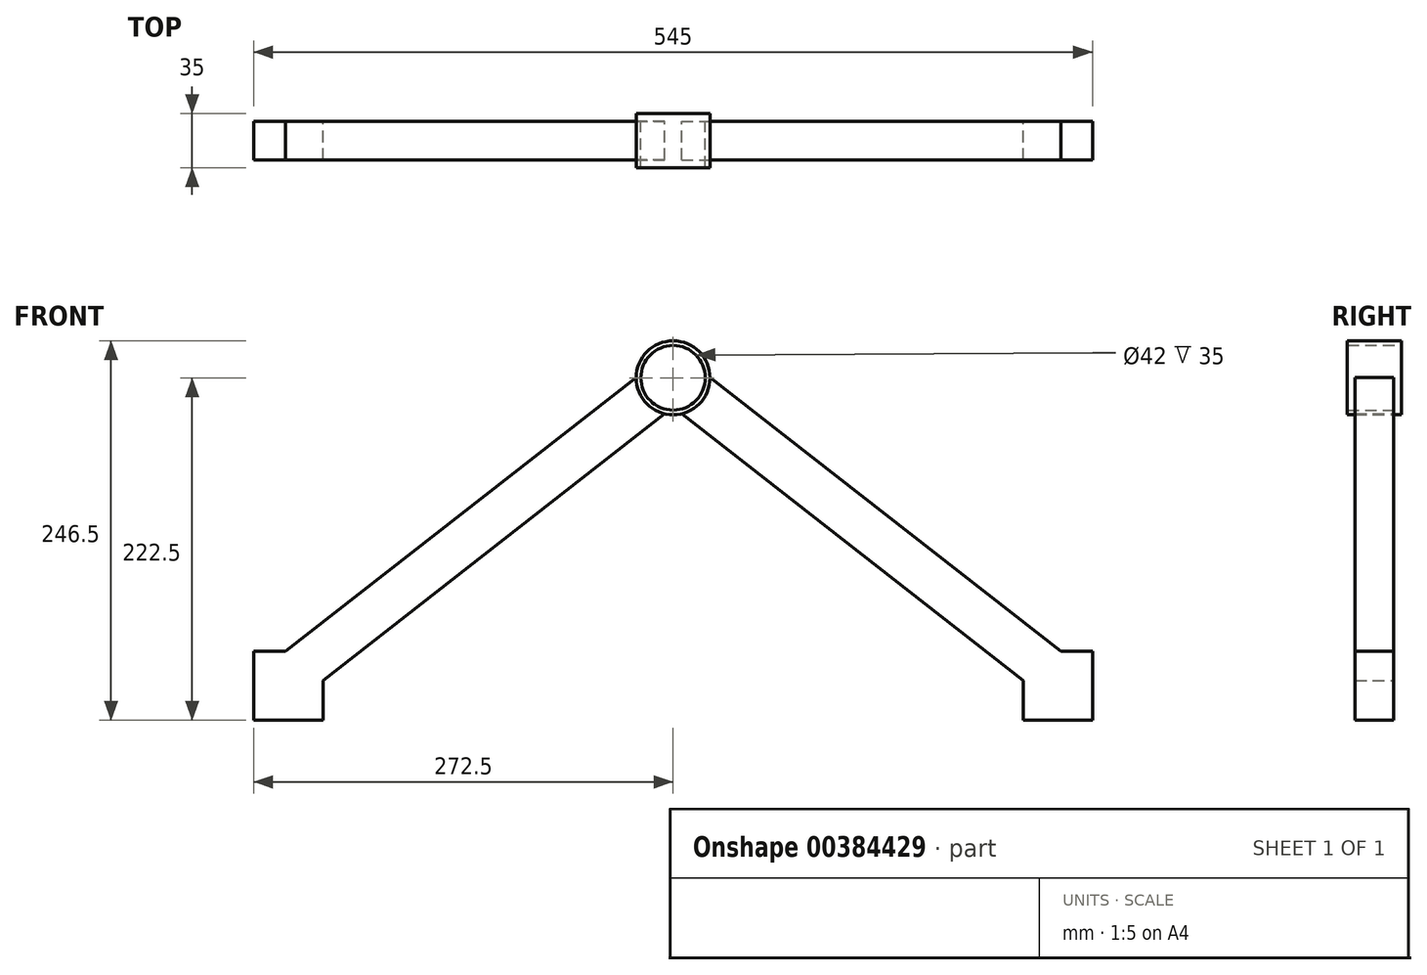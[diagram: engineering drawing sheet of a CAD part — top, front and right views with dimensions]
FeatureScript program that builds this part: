
annotation { "Feature Type Name" : "Feature", "Feature Type Description" : "" }
export const myFeature = defineFeature(function(context is Context, id is Id, definition is map)
    precondition{}
    {
        {
            var Q0;
            Q0=qCreatedBy(makeId("Front.planeOp"),FACE);
            var sketch = newSketch(context, id + "F0", { "sketchPlane" : qUnion([Q0])});
            skCircle(sketch, "E0", {"center": v(0, 0) * mm, "radius": 21 * mm});
            skCircle(sketch, "E1", {"center": v(0, 0) * mm, "radius": 24 * mm});
            skSolve(sketch);
        }
        {
            var Q0;
            Q0=makeQuery(id+"F0.imprint","IMPRINT",FACE,{"disambiguationData":[TD([[makeQuery(id+"F0.imprint","IMPRINT",EDGE,{"derivedFrom":sQuery(id+"F0.wireOp",EDGE,"E0")}),-1.0]])]});
            extrude(context, id + "F1", {"entities" : qUnion([Q0]), "endBound" : BoundingType.SYMMETRIC, "depth" : 35 * mm});
        }
        {
            var Q0;
            Q0=qCreatedBy(makeId("Front.planeOp"),FACE);
            var sketch = newSketch(context, id + "F2", { "sketchPlane" : qUnion([Q0])});
            skLineSegment(sketch, "E2.bottom", {"start": v(-227.5, -222.5) * mm, "end": v(-272.5, -222.5) * mm});
            skLineSegment(sketch, "E2.top", {"start": v(-251.88, -177.5) * mm, "end": v(-272.5, -177.5) * mm});
            skLineSegment(sketch, "E2.left", {"start": v(-227.5, -222.5) * mm, "end": v(-227.5, -196.53) * mm});
            skLineSegment(sketch, "E2.right", {"start": v(-272.5, -222.5) * mm, "end": v(-272.5, -177.5) * mm});
            skPoint(sketch, "E2.middle", {"position": v(-250, -200) * mm});
            skLineSegment(sketch, "E3", {"start": v(-28.15, -2.94) * mm, "end": v(-9.7, -26.59) * mm, "construction": true});
            skLineSegment(sketch, "E4", {"start": v(-9.7, -26.59) * mm, "end": v(-218.27, -189.33) * mm});
            skLineSegment(sketch, "E5", {"start": v(-218.27, -189.33) * mm, "end": v(-236.73, -165.67) * mm, "construction": true});
            skLineSegment(sketch, "E6", {"start": v(-236.73, -165.67) * mm, "end": v(-28.15, -2.94) * mm});
            skLineSegment(sketch, "E7", {"start": v(-227.5, -177.5) * mm, "end": v(0, 0) * mm, "construction": true});
            skLineSegment(sketch, "E8", {"start": v(0, 0) * mm, "end": v(0, 148.34) * mm, "construction": true});
            skLineSegment(sketch, "E9.MirrorCS", {"start": v(218.27, -189.33) * mm, "end": v(236.73, -165.67) * mm, "construction": true});
            skLineSegment(sketch, "E10.MirrorCS", {"start": v(28.15, -2.94) * mm, "end": v(9.7, -26.59) * mm, "construction": true});
            skPoint(sketch, "E11.MirrorP", {"position": v(250, -200) * mm});
            skLineSegment(sketch, "E12.MirrorCS", {"start": v(236.73, -165.67) * mm, "end": v(28.15, -2.94) * mm});
            skLineSegment(sketch, "E13.MirrorCS", {"start": v(227.5, -222.5) * mm, "end": v(272.5, -222.5) * mm});
            skLineSegment(sketch, "E14.MirrorCS", {"start": v(251.88, -177.5) * mm, "end": v(272.5, -177.5) * mm});
            skLineSegment(sketch, "E15.MirrorCS", {"start": v(9.7, -26.59) * mm, "end": v(218.27, -189.33) * mm});
            skLineSegment(sketch, "E16.MirrorCS", {"start": v(272.5, -222.5) * mm, "end": v(272.5, -177.5) * mm});
            skLineSegment(sketch, "E17.MirrorCS", {"start": v(227.5, -222.5) * mm, "end": v(227.5, -196.53) * mm});
            skLineSegment(sketch, "E18.MirrorCS", {"start": v(227.5, -177.5) * mm, "end": v(0, 0) * mm, "construction": true});
            skLineSegment(sketch, "E19", {"start": v(-28.15, -2.94) * mm, "end": v(-24, 0.3) * mm});
            skLineSegment(sketch, "E20", {"start": v(-9.7, -26.59) * mm, "end": v(-5.54, -23.35) * mm});
            skArc(sketch, "E21", {"start": v(-24, 0.3) * mm, "mid": v(-18.92, -14.76) * mm, "end": v(-5.54, -23.35) * mm});
            skLineSegment(sketch, "E22", {"start": v(9.7, -26.59) * mm, "end": v(5.54, -23.35) * mm});
            skLineSegment(sketch, "E23", {"start": v(28.15, -2.94) * mm, "end": v(24, 0.3) * mm});
            skArc(sketch, "E24.trimOffspring", {"start": v(5.54, -23.35) * mm, "mid": v(18.92, -14.76) * mm, "end": v(24, 0.3) * mm});
            skLineSegment(sketch, "E25", {"start": v(-236.73, -165.67) * mm, "end": v(-251.88, -177.5) * mm});
            skLineSegment(sketch, "E26", {"start": v(-218.27, -189.33) * mm, "end": v(-227.5, -196.53) * mm});
            skLineSegment(sketch, "E27", {"start": v(-227.5, -196.53) * mm, "end": v(-227.5, -177.5) * mm, "construction": true});
            skLineSegment(sketch, "E28", {"start": v(-251.88, -177.5) * mm, "end": v(-227.5, -177.5) * mm, "construction": true});
            skLineSegment(sketch, "E29", {"start": v(218.27, -189.33) * mm, "end": v(227.5, -196.53) * mm});
            skLineSegment(sketch, "E30", {"start": v(236.73, -165.67) * mm, "end": v(251.88, -177.5) * mm});
            skLineSegment(sketch, "E31", {"start": v(227.5, -196.53) * mm, "end": v(227.5, -177.5) * mm, "construction": true});
            skPoint(sketch, "E32", {"position": v(227.5, -196.53) * mm});
            skPoint(sketch, "E33", {"position": v(251.88, -177.5) * mm});
            skLineSegment(sketch, "E34", {"start": v(251.88, -177.5) * mm, "end": v(227.5, -177.5) * mm, "construction": true});
            skSolve(sketch);
        }
        {
            var Q0;
            Q0=makeQuery(id+"F2.imprint","IMPRINT",FACE,{"disambiguationData":[TD([[makeQuery(id+"F2.imprint","IMPRINT",EDGE,{"derivedFrom":sQuery(id+"F2.wireOp",EDGE,"E9.MirrorCS")}),1.0]])]});
            var Q1;
            Q1=makeQuery(id+"F2.imprint","IMPRINT",FACE,{"disambiguationData":[TD([[makeQuery(id+"F2.imprint","IMPRINT",EDGE,{"derivedFrom":sQuery(id+"F2.wireOp",EDGE,"E4")}),-1.0]])]});
            var Q2;
            Q2=makeQuery(id+"F2.imprint","IMPRINT",FACE,{"disambiguationData":[TD([[makeQuery(id+"F2.imprint","IMPRINT",EDGE,{"derivedFrom":sQuery(id+"F2.wireOp",EDGE,"E12.MirrorCS")}),1.0]])]});
            extrude(context, id + "F3", {"entities" : qUnion([Q0, Q1, Q2]), "operationType" : NewBodyOperationType.ADD, "endBound" : BoundingType.SYMMETRIC, "depth" : 25 * mm});
        }
    });
